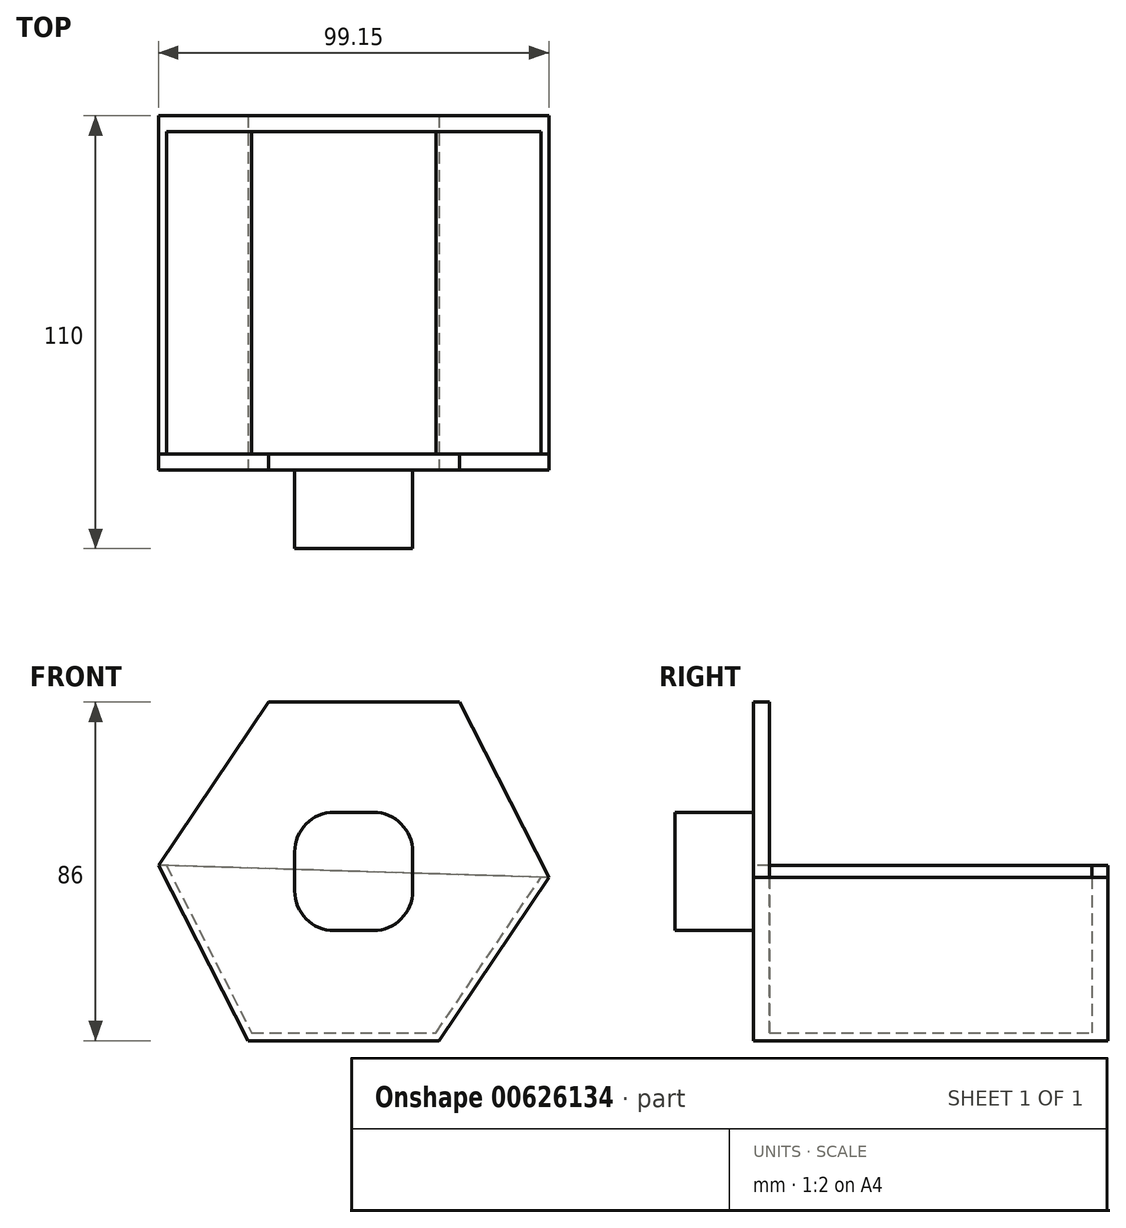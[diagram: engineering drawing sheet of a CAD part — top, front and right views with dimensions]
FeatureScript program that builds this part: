
annotation { "Feature Type Name" : "Feature", "Feature Type Description" : "" }
export const myFeature = defineFeature(function(context is Context, id is Id, definition is map)
    precondition{}
    {
        {
            var Q0;
            Q0=qCreatedBy(makeId("Front.planeOp"),FACE);
            var sketch = newSketch(context, id + "F0", { "sketchPlane" : qUnion([Q0])});
            skLineSegment(sketch, "E0", {"start": v(0, 0) * mm, "end": v(48.49, 0) * mm});
            skLineSegment(sketch, "E1", {"start": v(48.49, 0) * mm, "end": v(76.45, 41.45) * mm});
            skLineSegment(sketch, "E2", {"start": v(76.45, 41.45) * mm, "end": v(53.75, 86) * mm});
            skLineSegment(sketch, "E3", {"start": v(53.75, 86) * mm, "end": v(5.26, 86) * mm});
            skLineSegment(sketch, "E4", {"start": v(5.26, 86) * mm, "end": v(-22.7, 44.55) * mm});
            skLineSegment(sketch, "E5", {"start": v(-22.7, 44.55) * mm, "end": v(0, 0) * mm});
            skSolve(sketch);
        }
        {
            var Q0;
            Q0 = qSketchRegion(id + "F0", true);
            extrude(context, id + "F1", {"entities" : qUnion([Q0]), "oppositeDirection" : true, "depth" : 90 * mm, "offsetDistance" : 25 * mm});
        }
        {
            var Q0;
            Q0=makeQuery(id+"F1.opExtrude","CAP_FACE",FACE,{"disambiguationData":[OSD([sQuery(id+"F0.wireOp",EDGE,"E0"),sQuery(id+"F0.wireOp",EDGE,"E1"),sQuery(id+"F0.wireOp",EDGE,"E2"),sQuery(id+"F0.wireOp",EDGE,"E3"),sQuery(id+"F0.wireOp",EDGE,"E4"),sQuery(id+"F0.wireOp",EDGE,"E5")])],"isStart":false});
            var sketch = newSketch(context, id + "F2", { "sketchPlane" : qUnion([Q0])});
            skLineSegment(sketch, "E6", {"start": v(-76.45, 41.45) * mm, "end": v(22.7, 44.55) * mm});
            skLineSegment(sketch, "E7", {"start": v(22.7, 44.55) * mm, "end": v(-5.26, 86) * mm});
            skLineSegment(sketch, "E8", {"start": v(-5.26, 86) * mm, "end": v(-53.75, 86) * mm});
            skLineSegment(sketch, "E9", {"start": v(-53.75, 86) * mm, "end": v(-76.45, 41.45) * mm});
            skSolve(sketch);
        }
        {
            var Q0;
            Q0 = qSketchRegion(id + "F2", true);
            extrude(context, id + "F3", {"entities" : qUnion([Q0]), "operationType" : NewBodyOperationType.REMOVE, "oppositeDirection" : true, "depth" : 86 * mm, "offsetDistance" : 25 * mm});
        }
        {
            var Q0;
            Q0=makeQuery(id+"F1.opExtrude","CAP_FACE",FACE,{"disambiguationData":[OSD([sQuery(id+"F0.wireOp",EDGE,"E0"),sQuery(id+"F0.wireOp",EDGE,"E1"),sQuery(id+"F0.wireOp",EDGE,"E2"),sQuery(id+"F0.wireOp",EDGE,"E3"),sQuery(id+"F0.wireOp",EDGE,"E4"),sQuery(id+"F0.wireOp",EDGE,"E5")])],"isStart":false});
            var sketch = newSketch(context, id + "F4", { "sketchPlane" : qUnion([Q0])});
            skLineSegment(sketch, "E10", {"start": v(-47.8, 2) * mm, "end": v(-0.95, 2) * mm});
            skLineSegment(sketch, "E11", {"start": v(-0.95, 2) * mm, "end": v(20.7, 44.49) * mm});
            skLineSegment(sketch, "E12", {"start": v(20.7, 44.49) * mm, "end": v(-74.45, 41.51) * mm});
            skLineSegment(sketch, "E13", {"start": v(-74.45, 41.51) * mm, "end": v(-47.8, 2) * mm});
            skSolve(sketch);
        }
        {
            var Q0;
            Q0 = qSketchRegion(id + "F4", true);
            extrude(context, id + "F5", {"entities" : qUnion([Q0]), "operationType" : NewBodyOperationType.REMOVE, "oppositeDirection" : true, "depth" : 86 * mm, "offsetDistance" : 25 * mm});
        }
        {
            var Q0;
            Q0=makeQuery(id+"F1.opExtrude","CAP_FACE",FACE,{"disambiguationData":[OSD([sQuery(id+"F0.wireOp",EDGE,"E0"),sQuery(id+"F0.wireOp",EDGE,"E1"),sQuery(id+"F0.wireOp",EDGE,"E2"),sQuery(id+"F0.wireOp",EDGE,"E3"),sQuery(id+"F0.wireOp",EDGE,"E4"),sQuery(id+"F0.wireOp",EDGE,"E5")])],"isStart":false});
            var sketch = newSketch(context, id + "F6", { "sketchPlane" : qUnion([Q0])});
            skLineSegment(sketch, "E14", {"start": v(-76.45, 41.45) * mm, "end": v(22.7, 44.55) * mm});
            skLineSegment(sketch, "E15", {"start": v(22.7, 44.55) * mm, "end": v(0, 0) * mm});
            skLineSegment(sketch, "E16", {"start": v(0, 0) * mm, "end": v(-48.49, 0) * mm});
            skLineSegment(sketch, "E17", {"start": v(-48.49, 0) * mm, "end": v(-76.45, 41.45) * mm});
            skSolve(sketch);
        }
        {
            var Q0;
            Q0 = qSketchRegion(id + "F6", true);
            extrude(context, id + "F7", {"entities" : qUnion([Q0]), "operationType" : NewBodyOperationType.ADD, "oppositeDirection" : true, "depth" : 4 * mm, "offsetDistance" : 25 * mm});
        }
        {
            var Q0;
            Q0=makeQuery(id+"F1.opExtrude","CAP_FACE",FACE,{"disambiguationData":[OSD([sQuery(id+"F0.wireOp",EDGE,"E0"),sQuery(id+"F0.wireOp",EDGE,"E1"),sQuery(id+"F0.wireOp",EDGE,"E2"),sQuery(id+"F0.wireOp",EDGE,"E3"),sQuery(id+"F0.wireOp",EDGE,"E4"),sQuery(id+"F0.wireOp",EDGE,"E5")])],"isStart":true});
            var sketch = newSketch(context, id + "F8", { "sketchPlane" : qUnion([Q0])});
            skCircle(sketch, "E18", {"center": v(26.88, 43) * mm, "radius": 15 * mm});
            skPoint(sketch, "E19.oppositeSnap0", {"position": v(62.47, 20.72) * mm});
            skLineSegment(sketch, "E20.bottom", {"start": v(11.88, 58) * mm, "end": v(41.88, 58) * mm});
            skLineSegment(sketch, "E20.top", {"start": v(11.88, 28) * mm, "end": v(41.88, 28) * mm});
            skLineSegment(sketch, "E20.left", {"start": v(11.88, 58) * mm, "end": v(11.88, 28) * mm});
            skLineSegment(sketch, "E20.right", {"start": v(41.88, 58) * mm, "end": v(41.88, 28) * mm});
            skSolve(sketch);
        }
        {
            var Q0;
            {var subQ0=sQuery(id+"F8.wireOp",EDGE,"E20.right");var subQ1=sQuery(id+"F8.wireOp",EDGE,"E18");var subQ2=makeQuery(id+"F8.imprint","INTERSECT",VERTEX,{"derivedFrom":[subQ1,subQ0]});Q0=makeQuery(id+"F8.imprint","IMPRINT",FACE,{"disambiguationData":[TD([[makeQuery(id+"F8.imprint","IMPRINT",EDGE,{"disambiguationData":[TD([[subQ2,1.0]])],"derivedFrom":subQ1}),-1.0]])]});}
            var Q1;
            {var subQ0=sQuery(id+"F8.wireOp",EDGE,"E20.bottom");var subQ1=sQuery(id+"F8.wireOp",EDGE,"E18");var subQ2=makeQuery(id+"F8.imprint","INTERSECT",VERTEX,{"derivedFrom":[subQ1,subQ0]});Q1=makeQuery(id+"F8.imprint","IMPRINT",FACE,{"disambiguationData":[TD([[makeQuery(id+"F8.imprint","IMPRINT",EDGE,{"disambiguationData":[TD([[subQ2,1.0]])],"derivedFrom":subQ1}),-1.0]])]});}
            var Q2;
            {var subQ0=sQuery(id+"F8.wireOp",EDGE,"E20.bottom");var subQ1=sQuery(id+"F8.wireOp",EDGE,"E18");var subQ2=makeQuery(id+"F8.imprint","INTERSECT",VERTEX,{"derivedFrom":[subQ1,subQ0]});Q2=makeQuery(id+"F8.imprint","IMPRINT",FACE,{"disambiguationData":[TD([[makeQuery(id+"F8.imprint","IMPRINT",EDGE,{"disambiguationData":[TD([[subQ2,-1.0]])],"derivedFrom":subQ1}),-1.0]])]});}
            var Q3;
            {var subQ0=sQuery(id+"F8.wireOp",EDGE,"E18");var subQ1=makeQuery(id+"F8.imprint","INTERSECT",VERTEX,{"derivedFrom":[subQ0,sQuery(id+"F8.wireOp",EDGE,"E20.bottom")]});Q3=makeQuery(id+"F8.imprint","IMPRINT",FACE,{"disambiguationData":[TD([[makeQuery(id+"F8.imprint","IMPRINT",EDGE,{"disambiguationData":[TD([[subQ1,1.0]])],"derivedFrom":subQ0}),1.0]])]});}
            var Q4;
            {var subQ0=sQuery(id+"F8.wireOp",EDGE,"E20.left");var subQ1=sQuery(id+"F8.wireOp",EDGE,"E18");var subQ2=makeQuery(id+"F8.imprint","INTERSECT",VERTEX,{"derivedFrom":[subQ1,subQ0]});Q4=makeQuery(id+"F8.imprint","IMPRINT",FACE,{"disambiguationData":[TD([[makeQuery(id+"F8.imprint","IMPRINT",EDGE,{"disambiguationData":[TD([[subQ2,-1.0]])],"derivedFrom":subQ1}),-1.0]])]});}
            extrude(context, id + "F9", {"entities" : qUnion([Q0, Q1, Q2, Q3, Q4]), "operationType" : NewBodyOperationType.ADD, "depth" : 20 * mm, "offsetDistance" : 25 * mm});
        }
        {
            var Q0;
            Q0=makeQuery(id+"F9.opExtrude","SWEPT_EDGE",EDGE,{"disambiguationData":[OSD([sQuery(id+"F8.wireOp",EDGE,"E20.bottom"),sQuery(id+"F8.wireOp",EDGE,"E20.left")])]});
            var Q1;
            Q1=makeQuery(id+"F9.opExtrude","SWEPT_EDGE",EDGE,{"disambiguationData":[OSD([sQuery(id+"F8.wireOp",EDGE,"E20.bottom"),sQuery(id+"F8.wireOp",EDGE,"E20.right")])]});
            var Q2;
            Q2=makeQuery(id+"F9.opExtrude","SWEPT_EDGE",EDGE,{"disambiguationData":[OSD([sQuery(id+"F8.wireOp",EDGE,"E20.top"),sQuery(id+"F8.wireOp",EDGE,"E20.left")])]});
            var Q3;
            Q3=makeQuery(id+"F9.opExtrude","SWEPT_EDGE",EDGE,{"disambiguationData":[OSD([sQuery(id+"F8.wireOp",EDGE,"E20.top"),sQuery(id+"F8.wireOp",EDGE,"E20.right")])]});
            fillet(context, id + "F10", {"entities" : qUnion([Q0, Q1, Q2, Q3]), "radius" : 10 * mm, "tangentPropagation" : true, "allowEdgeOverflow" : false});
        }
    });
